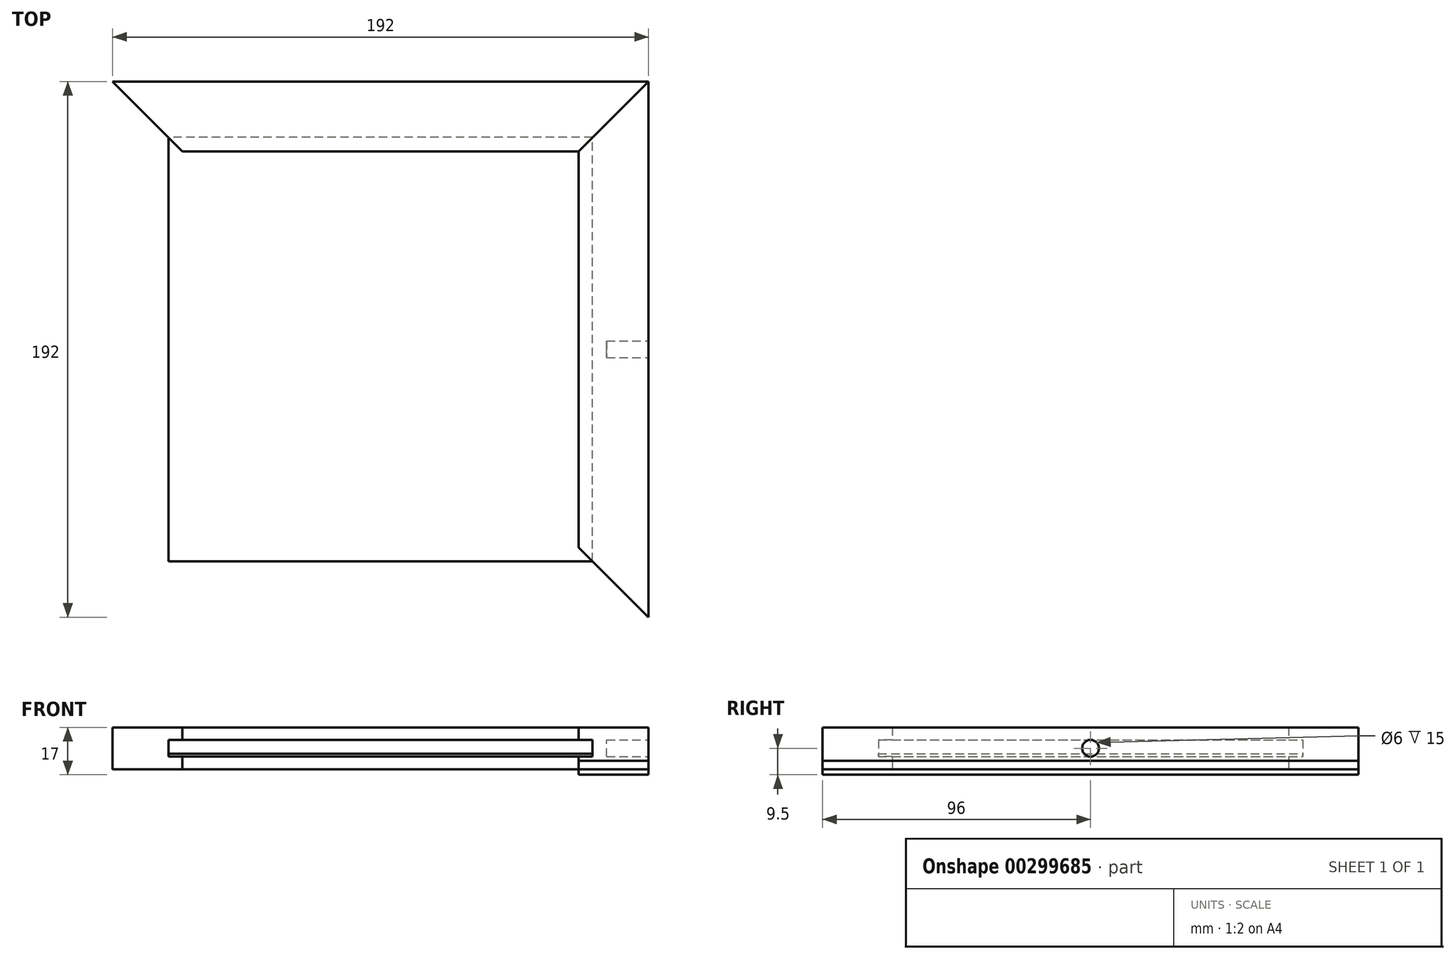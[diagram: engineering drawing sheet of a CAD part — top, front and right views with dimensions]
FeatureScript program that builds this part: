
annotation { "Feature Type Name" : "Feature", "Feature Type Description" : "" }
export const myFeature = defineFeature(function(context is Context, id is Id, definition is map)
    precondition{}
    {
        {
            var Q0;
            Q0=qCreatedBy(makeId("Top.planeOp"),FACE);
            var sketch = newSketch(context, id + "F0", { "sketchPlane" : qUnion([Q0])});
            skLineSegment(sketch, "E0.bottom", {"start": v(71, -71) * mm, "end": v(-71, -71) * mm});
            skLineSegment(sketch, "E0.top", {"start": v(71, 71) * mm, "end": v(-71, 71) * mm});
            skLineSegment(sketch, "E0.left", {"start": v(71, -71) * mm, "end": v(71, 71) * mm});
            skLineSegment(sketch, "E0.right", {"start": v(-71, -71) * mm, "end": v(-71, 71) * mm});
            skPoint(sketch, "E0.middle", {"position": v(0, 0) * mm});
            skLineSegment(sketch, "E1.top", {"start": v(96, 96) * mm, "end": v(-96, 96) * mm});
            skLineSegment(sketch, "E1.left", {"start": v(96, -96) * mm, "end": v(96, 96) * mm});
            skLineSegment(sketch, "E2", {"start": v(-71, 71) * mm, "end": v(-96, 96) * mm});
            skLineSegment(sketch, "E3", {"start": v(71, 71) * mm, "end": v(96, 96) * mm});
            skLineSegment(sketch, "E4.bottom", {"start": v(76, -76) * mm, "end": v(-76, -76) * mm});
            skLineSegment(sketch, "E4.top", {"start": v(76, 76) * mm, "end": v(-76, 76) * mm});
            skLineSegment(sketch, "E4.left", {"start": v(76, -76) * mm, "end": v(76, 76) * mm});
            skLineSegment(sketch, "E4.right", {"start": v(-76, -76) * mm, "end": v(-76, 76) * mm});
            skLineSegment(sketch, "E5", {"start": v(71, -71) * mm, "end": v(96, -96) * mm});
            skPoint(sketch, "E1.bottom.end.orphan", {"position": v(-96, -96) * mm});
            skSolve(sketch);
        }
        {
            var Q0;
            {var subQ0=sQuery(id+"F0.wireOp",EDGE,"E1.top");Q0=makeQuery(id+"F0.imprint","IMPRINT",FACE,{"disambiguationData":[TD([[makeQuery(id+"F0.imprint","IMPRINT",EDGE,{"derivedFrom":subQ0}),1.0]])]});}
            var Q1;
            {var subQ0=sQuery(id+"F0.wireOp",EDGE,"E0.top");Q1=makeQuery(id+"F0.imprint","IMPRINT",FACE,{"disambiguationData":[TD([[makeQuery(id+"F0.imprint","IMPRINT",EDGE,{"derivedFrom":subQ0}),-1.0]])]});}
            var Q2;
            Q2=sQuery(id+"F0.wireOp",EDGE,"E0.top");
            var Q3;
            Q3=sQuery(id+"F0.wireOp",EDGE,"E2");
            var Q4;
            Q4=sQuery(id+"F0.wireOp",EDGE,"E3");
            var Q5;
            Q5=sQuery(id+"F0.wireOp",EDGE,"E1.top");
            extrude(context, id + "F1", {"entities" : qUnion([Q0, Q1]), "surfaceEntities" : qUnion([Q2, Q3, Q4, Q5]), "endBound" : BoundingType.SYMMETRIC, "depth" : 15 * mm});
        }
        {
            var Q0;
            {var subQ0=sQuery(id+"F0.wireOp",EDGE,"E1.left");Q0=makeQuery(id+"F0.imprint","IMPRINT",FACE,{"disambiguationData":[TD([[makeQuery(id+"F0.imprint","IMPRINT",EDGE,{"derivedFrom":subQ0}),1.0]])]});}
            var Q1;
            {var subQ0=sQuery(id+"F0.wireOp",EDGE,"E0.left");Q1=makeQuery(id+"F0.imprint","IMPRINT",FACE,{"disambiguationData":[TD([[makeQuery(id+"F0.imprint","IMPRINT",EDGE,{"derivedFrom":subQ0}),-1.0]])]});}
            extrude(context, id + "F2", {"entities" : qUnion([Q0, Q1]), "endBound" : BoundingType.SYMMETRIC, "depth" : 15 * mm});
        }
        {
            var Q0;
            {var subQ0=sQuery(id+"F0.wireOp",EDGE,"E0.top");Q0=makeQuery(id+"F0.imprint","IMPRINT",FACE,{"disambiguationData":[TD([[makeQuery(id+"F0.imprint","IMPRINT",EDGE,{"derivedFrom":subQ0}),-1.0]])]});}
            extrude(context, id + "F3", {"entities" : qUnion([Q0]), "operationType" : NewBodyOperationType.REMOVE, "endBound" : BoundingType.SYMMETRIC, "oppositeDirection" : true, "depth" : 6 * mm});
        }
        {
            var Q0;
            {var subQ0=sQuery(id+"F0.wireOp",EDGE,"E0.left");Q0=makeQuery(id+"F0.imprint","IMPRINT",FACE,{"disambiguationData":[TD([[makeQuery(id+"F0.imprint","IMPRINT",EDGE,{"derivedFrom":subQ0}),-1.0]])]});}
            extrude(context, id + "F4", {"entities" : qUnion([Q0]), "operationType" : NewBodyOperationType.REMOVE, "endBound" : BoundingType.SYMMETRIC, "depth" : 6 * mm});
        }
        {
            var Q0;
            Q0=makeQuery(id+"F2.opExtrude","SWEPT_FACE",FACE,{"disambiguationData":[OSD([sQuery(id+"F0.wireOp",EDGE,"E1.left")])]});
            var sketch = newSketch(context, id + "F5", { "sketchPlane" : qUnion([Q0])});
            skCircle(sketch, "E6", {"center": v(0, 0) * mm, "radius": 3 * mm});
            skSolve(sketch);
        }
        {
            var Q0;
            Q0=qSketchRegion(id+"F5",true);
            extrude(context, id + "F6", {"entities" : qUnion([Q0]), "operationType" : NewBodyOperationType.REMOVE, "oppositeDirection" : true, "depth" : 15 * mm});
        }
        {
            var Q0;
            Q0=qCreatedBy(makeId("Top.planeOp"),FACE);
            var sketch = newSketch(context, id + "F7", { "sketchPlane" : qUnion([Q0])});
            skLineSegment(sketch, "E7.bottom", {"start": v(76, -76) * mm, "end": v(-76, -76) * mm});
            skLineSegment(sketch, "E7.top", {"start": v(76, 76) * mm, "end": v(-76, 76) * mm});
            skLineSegment(sketch, "E7.left", {"start": v(76, -76) * mm, "end": v(76, 76) * mm});
            skLineSegment(sketch, "E7.right", {"start": v(-76, -76) * mm, "end": v(-76, 76) * mm});
            skPoint(sketch, "E7.middle", {"position": v(0, 0) * mm});
            skSolve(sketch);
        }
        {
            var Q0;
            Q0=qSketchRegion(id+"F7",true);
            var Q1;
            Q1=makeQuery(id+"F2.opExtrude","CAP_FACE",FACE,{"disambiguationData":[OSD([sQuery(id+"F0.wireOp",EDGE,"E0.left"),sQuery(id+"F0.wireOp",EDGE,"E1.left"),sQuery(id+"F0.wireOp",EDGE,"E3"),sQuery(id+"F0.wireOp",EDGE,"E5")])],"isStart":true});
            extrude(context, id + "F8", {"entities" : qUnion([Q0, Q1]), "depth" : 3 * mm, "hasSecondDirection" : true, "secondDirectionOppositeDirection" : true, "secondDirectionDepth" : 2 * mm});
        }
        {
            var Q0;
            Q0=makeQuery(id+"F8.opExtrude","CAP_FACE",FACE,{"disambiguationData":[OSD([sQuery(id+"F7.wireOp",EDGE,"E7.bottom"),sQuery(id+"F7.wireOp",EDGE,"E7.top"),sQuery(id+"F7.wireOp",EDGE,"E7.left"),sQuery(id+"F7.wireOp",EDGE,"E7.right")])],"isStart":true});
            var sketch = newSketch(context, id + "F9", { "sketchPlane" : qUnion([Q0])});
            skSolve(sketch);
        }
        {
            var Q0;
            Q0=makeQuery(id+"F9.imprint","IMPRINT",FACE,{"disambiguationData":[TD([[makeQuery(id+"F9.imprint","IMPRINT",EDGE,{"derivedFrom":makeQuery(id+"F8.opExtrude","CAP_EDGE",EDGE,{"disambiguationData":[OSD([sQuery(id+"F7.wireOp",EDGE,"E7.bottom")])],"isStart":true})}),1.0]])]});
            var sketch = newSketch(context, id + "F10", { "sketchPlane" : qUnion([Q0])});
            skLineSegment(sketch, "E8.0.0", {"start": v(76, -76) * mm, "end": v(76, 76) * mm});
            skLineSegment(sketch, "E8.0.1", {"start": v(76, 76) * mm, "end": v(-76, 76) * mm});
            skLineSegment(sketch, "E8.0.2", {"start": v(-76, 76) * mm, "end": v(-76, -76) * mm});
            skLineSegment(sketch, "E8.0.3", {"start": v(-76, -76) * mm, "end": v(76, -76) * mm});
            skSolve(sketch);
        }
        {
            var Q0;
            Q0=qSketchRegion(id+"F10",true);
            extrude(context, id + "F11", {"entities" : qUnion([Q0]), "depth" : 1 * mm});
        }
    });
